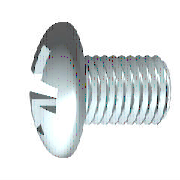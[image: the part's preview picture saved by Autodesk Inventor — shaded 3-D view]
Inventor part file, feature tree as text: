
AUTODESK INVENTOR PART (.ipt)
format: ipt  version: 2022 (Build 260153000, 153)  size: 283,136 bytes
history: native  units: mm (DEFAULTED — no unit token found)
features: other x2, plane x2, extrude x1
ambient origin geometry x7: Origin, YZ Plane, XZ Plane, X Axis, Y Axis, Z Axis, Center Point
bodies: Solid1 (feature_tree)
feature tree (5):
  other  "Базовый элемент"
  plane  "Work Plane1"
  extrude  "Паз"  Depth=3.5mm
  other  "Вырез"
  plane  "Work Plane3"
